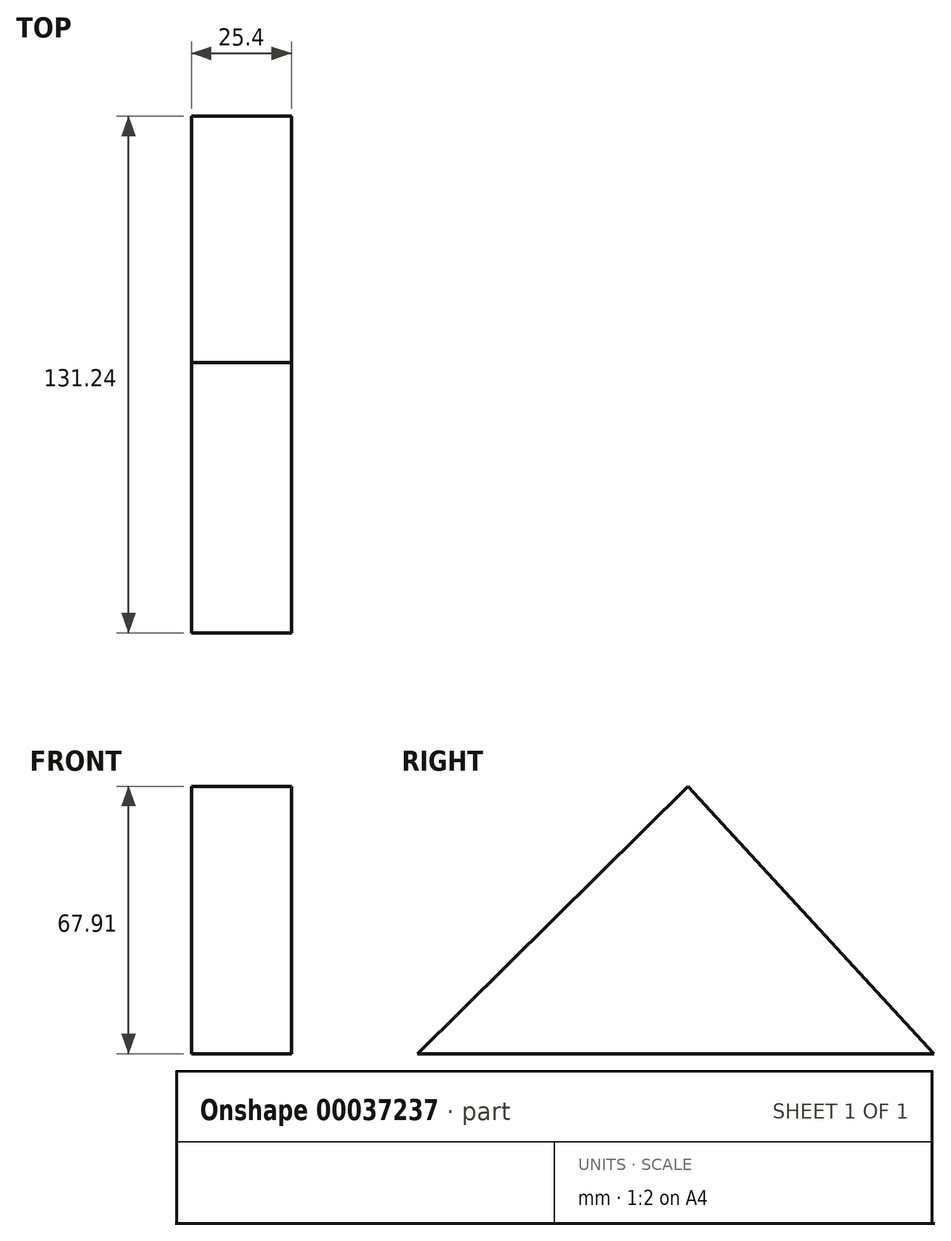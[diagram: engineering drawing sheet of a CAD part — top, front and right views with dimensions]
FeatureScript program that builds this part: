
annotation { "Feature Type Name" : "Feature", "Feature Type Description" : "" }
export const myFeature = defineFeature(function(context is Context, id is Id, definition is map)
    precondition{}
    {
        {
            var Q0;
            Q0=qCreatedBy(makeId("Right.planeOp"),FACE);
            var sketch = newSketch(context, id + "F0", { "sketchPlane" : qUnion([Q0])});
            skLineSegment(sketch, "E0", {"start": v(-68.74, 0) * mm, "end": v(0, 67.91) * mm});
            skLineSegment(sketch, "E1", {"start": v(0, 67.91) * mm, "end": v(62.5, 0) * mm});
            skLineSegment(sketch, "E2", {"start": v(62.5, 0) * mm, "end": v(-68.74, 0) * mm});
            skLineSegment(sketch, "E3", {"start": v(-68.74, 0) * mm, "end": v(-68.74, -55.45) * mm});
            skLineSegment(sketch, "E4", {"start": v(-68.74, -55.45) * mm, "end": v(-57, -55.45) * mm});
            skLineSegment(sketch, "E5", {"start": v(-57, -55.45) * mm, "end": v(-35.74, 0) * mm});
            skLineSegment(sketch, "E6", {"start": v(62.5, 0) * mm, "end": v(60.67, -56.36) * mm});
            skLineSegment(sketch, "E7", {"start": v(60.67, -56.36) * mm, "end": v(46.37, -55.9) * mm});
            skLineSegment(sketch, "E8", {"start": v(46.37, -55.9) * mm, "end": v(31.71, 0) * mm});
            skSolve(sketch);
        }
        {
            var Q0;
            {var subQ2=sQuery(id+"F0.wireOp",EDGE,"E0");Q0=makeQuery(id+"F0.imprint","IMPRINT",FACE,{"disambiguationData":[TD([[makeQuery(id+"F0.imprint","IMPRINT",EDGE,{"derivedFrom":subQ2}),-1.0]])]});}
            extrude(context, id + "F1", {"entities" : qUnion([Q0]), "depth" : 25.4 * mm});
        }
    });
